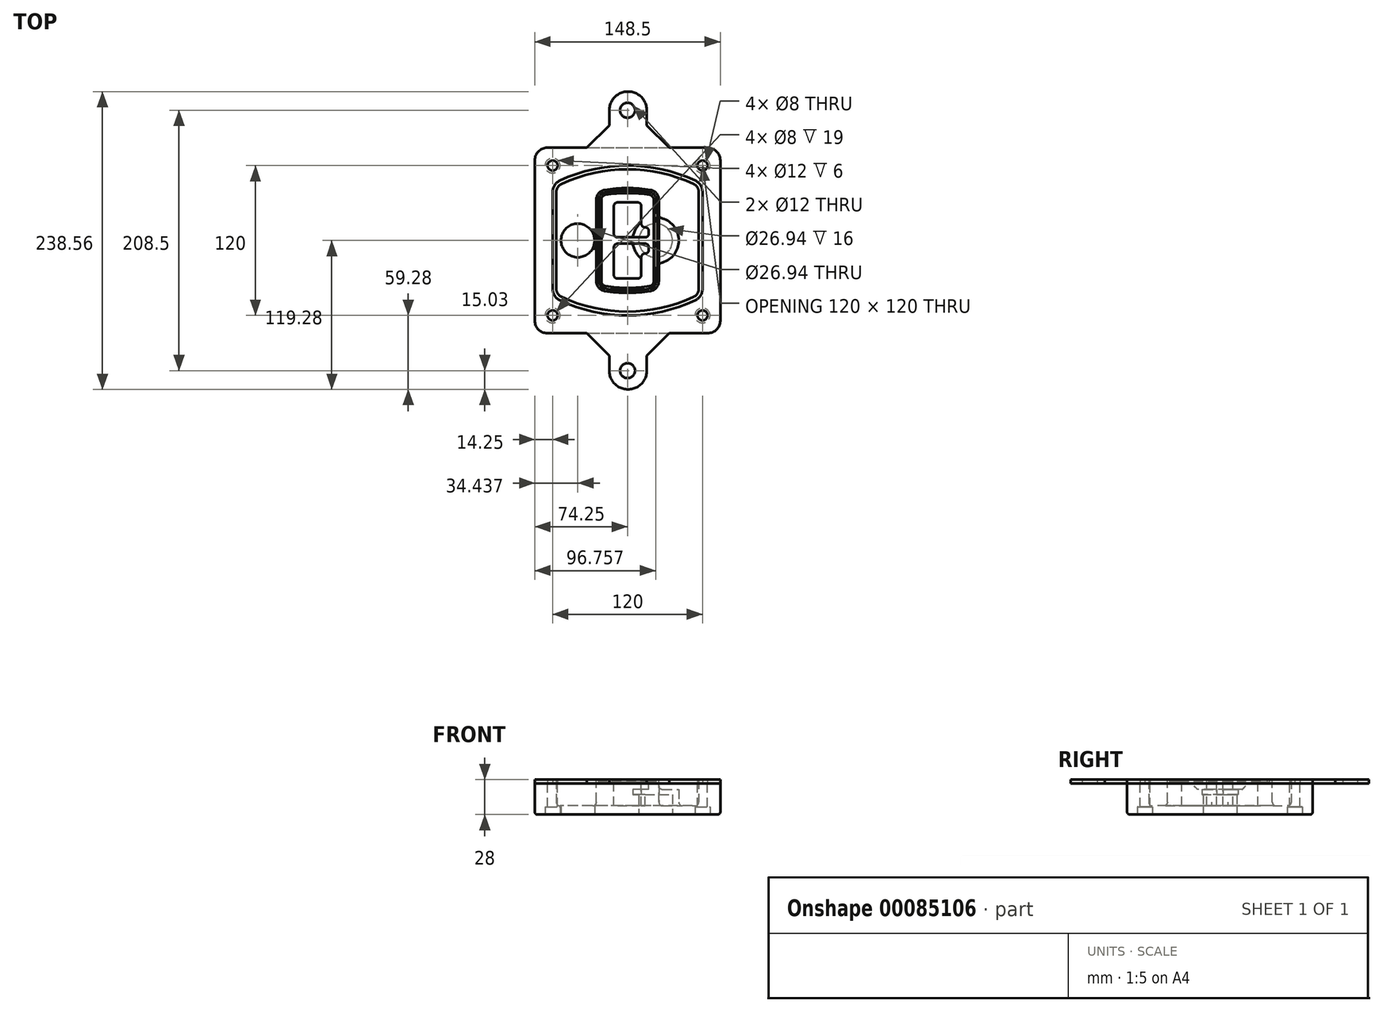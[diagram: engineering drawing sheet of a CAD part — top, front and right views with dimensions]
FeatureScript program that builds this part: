
annotation { "Feature Type Name" : "Feature", "Feature Type Description" : "" }
export const myFeature = defineFeature(function(context is Context, id is Id, definition is map)
    precondition{}
    {
        {
            var Q0;
            Q0=qCreatedBy(makeId("Top.planeOp"),FACE);
            var sketch = newSketch(context, id + "F0", { "sketchPlane" : qUnion([Q0])});
            skPoint(sketch, "E0.rect.middle", {"position": v(0, 0) * mm});
            skLineSegment(sketch, "E1.bottom", {"start": v(-64.25, -74.25) * mm, "end": v(64.25, -74.25) * mm});
            skLineSegment(sketch, "E1.top", {"start": v(-64.25, 74.25) * mm, "end": v(64.25, 74.25) * mm});
            skLineSegment(sketch, "E1.left", {"start": v(-74.25, -64.25) * mm, "end": v(-74.25, 64.25) * mm});
            skLineSegment(sketch, "E1.right", {"start": v(74.25, -64.25) * mm, "end": v(74.25, 64.25) * mm});
            skLineSegment(sketch, "E2", {"start": v(-74.25, 74.25) * mm, "end": v(74.25, -74.25) * mm, "construction": true});
            skLineSegment(sketch, "E3", {"start": v(74.25, 74.25) * mm, "end": v(-74.25, -74.25) * mm, "construction": true});
            skCircle(sketch, "E4", {"center": v(-60, 60) * mm, "radius": 4 * mm});
            skCircle(sketch, "E5", {"center": v(60, 60) * mm, "radius": 4 * mm});
            skCircle(sketch, "E6", {"center": v(60, -60) * mm, "radius": 4 * mm});
            skCircle(sketch, "E7", {"center": v(-60, -60) * mm, "radius": 4 * mm});
            skLineSegment(sketch, "E8", {"start": v(-60, 60) * mm, "end": v(60, 60) * mm, "construction": true});
            skLineSegment(sketch, "E9", {"start": v(60, 60) * mm, "end": v(60, -60) * mm, "construction": true});
            skLineSegment(sketch, "E10", {"start": v(60, -60) * mm, "end": v(-60, -60) * mm, "construction": true});
            skLineSegment(sketch, "E11", {"start": v(-60, -60) * mm, "end": v(-60, 60) * mm, "construction": true});
            skLineSegment(sketch, "E12", {"start": v(-60, 38.83) * mm, "end": v(-60, -38.83) * mm});
            skLineSegment(sketch, "E13", {"start": v(60, 38.83) * mm, "end": v(60, -38.83) * mm});
            skArc(sketch, "E14", {"start": v(54.26, 47.88) * mm, "mid": v(0, 60) * mm, "end": v(-54.26, 47.88) * mm});
            skArc(sketch, "E15", {"start": v(-54.26, -47.88) * mm, "mid": v(0, -60) * mm, "end": v(54.26, -47.88) * mm});
            skLineSegment(sketch, "E16", {"start": v(-60, 0) * mm, "end": v(60, 0) * mm, "construction": true});
            skPoint(sketch, "E17.visualSharp", {"position": v(-60, -45) * mm});
            skArc(sketch, "E17.filletArc", {"start": v(-60, -38.83) * mm, "mid": v(-58.44, -44.2) * mm, "end": v(-54.26, -47.88) * mm});
            skPoint(sketch, "E18.visualSharp", {"position": v(-60, 45) * mm});
            skArc(sketch, "E18.filletArc", {"start": v(-54.26, 47.88) * mm, "mid": v(-58.44, 44.2) * mm, "end": v(-60, 38.83) * mm});
            skPoint(sketch, "E19.visualSharp", {"position": v(60, 45) * mm});
            skArc(sketch, "E19.filletArc", {"start": v(60, 38.83) * mm, "mid": v(58.44, 44.2) * mm, "end": v(54.26, 47.88) * mm});
            skPoint(sketch, "E20.visualSharp", {"position": v(60, -45) * mm});
            skArc(sketch, "E20.filletArc", {"start": v(54.26, -47.88) * mm, "mid": v(58.44, -44.2) * mm, "end": v(60, -38.83) * mm});
            skPoint(sketch, "E21.visualSharp", {"position": v(-74.25, 74.25) * mm});
            skArc(sketch, "E21.filletArc", {"start": v(-64.25, 74.25) * mm, "mid": v(-71.32, 71.32) * mm, "end": v(-74.25, 64.25) * mm});
            skPoint(sketch, "E22.visualSharp", {"position": v(74.25, 74.25) * mm});
            skArc(sketch, "E22.filletArc", {"start": v(74.25, 64.25) * mm, "mid": v(71.32, 71.32) * mm, "end": v(64.25, 74.25) * mm});
            skPoint(sketch, "E23.visualSharp", {"position": v(74.25, -74.25) * mm});
            skArc(sketch, "E23.filletArc", {"start": v(64.25, -74.25) * mm, "mid": v(71.32, -71.32) * mm, "end": v(74.25, -64.25) * mm});
            skPoint(sketch, "E24.visualSharp", {"position": v(-74.25, -74.25) * mm});
            skArc(sketch, "E24.filletArc", {"start": v(-74.25, -64.25) * mm, "mid": v(-71.32, -71.32) * mm, "end": v(-64.25, -74.25) * mm});
            skArc(sketch, "E25.0", {"start": v(57, 38.83) * mm, "mid": v(55.9, 42.58) * mm, "end": v(52.98, 45.17) * mm});
            skLineSegment(sketch, "E25.1", {"start": v(57, 38.83) * mm, "end": v(57, -38.83) * mm});
            skArc(sketch, "E25.2", {"start": v(52.98, -45.17) * mm, "mid": v(55.9, -42.58) * mm, "end": v(57, -38.83) * mm});
            skArc(sketch, "E25.3", {"start": v(-52.98, -45.17) * mm, "mid": v(0, -57) * mm, "end": v(52.98, -45.17) * mm});
            skArc(sketch, "E25.4", {"start": v(-57, -38.83) * mm, "mid": v(-55.9, -42.58) * mm, "end": v(-52.98, -45.17) * mm});
            skArc(sketch, "E25.5", {"start": v(52.98, 45.17) * mm, "mid": v(0, 57) * mm, "end": v(-52.98, 45.17) * mm});
            skLineSegment(sketch, "E25.6", {"start": v(-57, 38.83) * mm, "end": v(-57, -38.83) * mm});
            skArc(sketch, "E25.7", {"start": v(-52.98, 45.17) * mm, "mid": v(-55.9, 42.58) * mm, "end": v(-57, 38.83) * mm});
            skArc(sketch, "E26.0", {"start": v(-55.96, 51.5) * mm, "mid": v(-61.82, 46.33) * mm, "end": v(-64, 38.83) * mm});
            skArc(sketch, "E26.1", {"start": v(55.96, 51.5) * mm, "mid": v(0, 64) * mm, "end": v(-55.96, 51.5) * mm});
            skArc(sketch, "E26.2", {"start": v(64, 38.83) * mm, "mid": v(61.82, 46.33) * mm, "end": v(55.96, 51.5) * mm});
            skLineSegment(sketch, "E26.3", {"start": v(64, 38.83) * mm, "end": v(64, -38.83) * mm});
            skArc(sketch, "E26.4", {"start": v(55.96, -51.5) * mm, "mid": v(61.82, -46.33) * mm, "end": v(64, -38.83) * mm});
            skLineSegment(sketch, "E26.5", {"start": v(-64, 38.83) * mm, "end": v(-64, -38.83) * mm});
            skArc(sketch, "E26.6", {"start": v(-55.96, -51.5) * mm, "mid": v(0, -64) * mm, "end": v(55.96, -51.5) * mm});
            skArc(sketch, "E26.7", {"start": v(-64, -38.83) * mm, "mid": v(-61.82, -46.33) * mm, "end": v(-55.96, -51.5) * mm});
            skSolve(sketch);
        }
        {
            var Q0;
            Q0=makeQuery(id+"F0.imprint","IMPRINT",FACE,{"disambiguationData":[TD([[makeQuery(id+"F0.imprint","IMPRINT",EDGE,{"derivedFrom":sQuery(id+"F0.wireOp",EDGE,"E1.bottom")}),1.0]])]});
            var Q1;
            Q1=makeQuery(id+"F0.imprint","IMPRINT",FACE,{"disambiguationData":[TD([[makeQuery(id+"F0.imprint","IMPRINT",EDGE,{"derivedFrom":sQuery(id+"F0.wireOp",EDGE,"E12")}),1.0]])]});
            var Q2;
            Q2=makeQuery(id+"F0.imprint","IMPRINT",FACE,{"disambiguationData":[TD([[makeQuery(id+"F0.imprint","IMPRINT",EDGE,{"derivedFrom":sQuery(id+"F0.wireOp",EDGE,"E25.0")}),1.0]])]});
            var Q3;
            Q3=makeQuery(id+"F0.imprint","IMPRINT",FACE,{"disambiguationData":[TD([[makeQuery(id+"F0.imprint","IMPRINT",EDGE,{"derivedFrom":sQuery(id+"F0.wireOp",EDGE,"E12")}),-1.0]])]});
            extrude(context, id + "F1", {"entities" : qUnion([Q0, Q1, Q2, Q3]), "oppositeDirection" : true, "depth" : 25 * mm});
        }
        {
            var Q0;
            Q0=makeQuery(id+"F0.imprint","IMPRINT",FACE,{"disambiguationData":[TD([[makeQuery(id+"F0.imprint","IMPRINT",EDGE,{"derivedFrom":sQuery(id+"F0.wireOp",EDGE,"E12")}),1.0]])]});
            extrude(context, id + "F2", {"entities" : qUnion([Q0]), "operationType" : NewBodyOperationType.ADD, "depth" : 3 * mm});
        }
        {
            var Q0;
            Q0=makeQuery(id+"F0.imprint","IMPRINT",FACE,{"disambiguationData":[TD([[makeQuery(id+"F0.imprint","IMPRINT",EDGE,{"derivedFrom":sQuery(id+"F0.wireOp",EDGE,"E25.0")}),1.0]])]});
            extrude(context, id + "F3", {"entities" : qUnion([Q0]), "operationType" : NewBodyOperationType.REMOVE, "oppositeDirection" : true, "depth" : 18 * mm});
        }
        {
            var Q0;
            Q0=makeQuery(id+"F2.opExtrude","CAP_FACE",FACE,{"disambiguationData":[OSD([sQuery(id+"F0.wireOp",EDGE,"E12"),sQuery(id+"F0.wireOp",EDGE,"E13"),sQuery(id+"F0.wireOp",EDGE,"E14"),sQuery(id+"F0.wireOp",EDGE,"E15"),sQuery(id+"F0.wireOp",EDGE,"E17.filletArc"),sQuery(id+"F0.wireOp",EDGE,"E18.filletArc"),sQuery(id+"F0.wireOp",EDGE,"E19.filletArc"),sQuery(id+"F0.wireOp",EDGE,"E20.filletArc"),sQuery(id+"F0.wireOp",EDGE,"E25.0"),sQuery(id+"F0.wireOp",EDGE,"E25.1"),sQuery(id+"F0.wireOp",EDGE,"E25.2"),sQuery(id+"F0.wireOp",EDGE,"E25.3"),sQuery(id+"F0.wireOp",EDGE,"E25.4"),sQuery(id+"F0.wireOp",EDGE,"E25.5"),sQuery(id+"F0.wireOp",EDGE,"E25.6"),sQuery(id+"F0.wireOp",EDGE,"E25.7")])],"isStart":false});
            var sketch = newSketch(context, id + "F4", { "sketchPlane" : qUnion([Q0])});
            skArc(sketch, "E27.0", {"start": v(-18.34, -40.45) * mm, "mid": v(0, -42) * mm, "end": v(18.34, -40.45) * mm});
            skArc(sketch, "E28.0", {"start": v(18.34, 40.45) * mm, "mid": v(0, 42) * mm, "end": v(-18.34, 40.45) * mm});
            skLineSegment(sketch, "E29", {"start": v(-25, 32.57) * mm, "end": v(-25, -32.57) * mm});
            skLineSegment(sketch, "E30", {"start": v(25, 32.57) * mm, "end": v(25, -32.57) * mm});
            skLineSegment(sketch, "E31", {"start": v(-25, 39.1) * mm, "end": v(25, 39.1) * mm, "construction": true});
            skLineSegment(sketch, "E32", {"start": v(-25, -39.1) * mm, "end": v(25, -39.1) * mm, "construction": true});
            skPoint(sketch, "E33.visualSharp", {"position": v(-25, 39.1) * mm});
            skArc(sketch, "E33.filletArc", {"start": v(-18.34, 40.45) * mm, "mid": v(-23.11, 37.73) * mm, "end": v(-25, 32.57) * mm});
            skPoint(sketch, "E34.visualSharp", {"position": v(25, 39.1) * mm});
            skArc(sketch, "E34.filletArc", {"start": v(25, 32.57) * mm, "mid": v(23.11, 37.73) * mm, "end": v(18.34, 40.45) * mm});
            skPoint(sketch, "E35.visualSharp", {"position": v(25, -39.1) * mm});
            skArc(sketch, "E35.filletArc", {"start": v(18.34, -40.45) * mm, "mid": v(23.11, -37.73) * mm, "end": v(25, -32.57) * mm});
            skPoint(sketch, "E36.visualSharp", {"position": v(-25, -39.1) * mm});
            skArc(sketch, "E36.filletArc", {"start": v(-25, -32.57) * mm, "mid": v(-23.11, -37.73) * mm, "end": v(-18.34, -40.45) * mm});
            skArc(sketch, "E37.0", {"start": v(52.98, 45.17) * mm, "mid": v(0, 57) * mm, "end": v(-52.98, 45.17) * mm});
            skArc(sketch, "E37.1", {"start": v(-52.98, 45.17) * mm, "mid": v(-55.9, 42.58) * mm, "end": v(-57, 38.83) * mm});
            skLineSegment(sketch, "E37.2", {"start": v(-57, 38.83) * mm, "end": v(-57, -38.83) * mm});
            skArc(sketch, "E37.3", {"start": v(-57, -38.83) * mm, "mid": v(-55.9, -42.58) * mm, "end": v(-52.98, -45.17) * mm});
            skArc(sketch, "E37.4", {"start": v(-52.98, -45.17) * mm, "mid": v(0, -57) * mm, "end": v(52.98, -45.17) * mm});
            skArc(sketch, "E37.5", {"start": v(52.98, -45.17) * mm, "mid": v(55.9, -42.58) * mm, "end": v(57, -38.83) * mm});
            skLineSegment(sketch, "E37.6", {"start": v(57, 38.83) * mm, "end": v(57, -38.83) * mm});
            skArc(sketch, "E37.7", {"start": v(57, 38.83) * mm, "mid": v(55.9, 42.58) * mm, "end": v(52.98, 45.17) * mm});
            skLineSegment(sketch, "E38.0", {"start": v(23, 32.57) * mm, "end": v(23, -32.57) * mm});
            skArc(sketch, "E38.1", {"start": v(18, -38.48) * mm, "mid": v(21.58, -36.44) * mm, "end": v(23, -32.57) * mm});
            skArc(sketch, "E38.2", {"start": v(-18, -38.48) * mm, "mid": v(0, -40) * mm, "end": v(18, -38.48) * mm});
            skArc(sketch, "E38.3", {"start": v(-23, -32.57) * mm, "mid": v(-21.58, -36.44) * mm, "end": v(-18, -38.48) * mm});
            skLineSegment(sketch, "E38.4", {"start": v(-23, 32.57) * mm, "end": v(-23, -32.57) * mm});
            skArc(sketch, "E38.5", {"start": v(23, 32.57) * mm, "mid": v(21.58, 36.44) * mm, "end": v(18, 38.48) * mm});
            skArc(sketch, "E38.6", {"start": v(-18, 38.48) * mm, "mid": v(-21.58, 36.44) * mm, "end": v(-23, 32.57) * mm});
            skArc(sketch, "E38.7", {"start": v(18, 38.48) * mm, "mid": v(0, 40) * mm, "end": v(-18, 38.48) * mm});
            skArc(sketch, "E39.0", {"start": v(21, 32.57) * mm, "mid": v(20.06, 35.15) * mm, "end": v(17.67, 36.5) * mm});
            skLineSegment(sketch, "E39.1", {"start": v(21, 32.57) * mm, "end": v(21, -32.57) * mm});
            skArc(sketch, "E39.2", {"start": v(17.67, -36.5) * mm, "mid": v(20.06, -35.15) * mm, "end": v(21, -32.57) * mm});
            skArc(sketch, "E39.3", {"start": v(-17.67, -36.5) * mm, "mid": v(0, -38) * mm, "end": v(17.67, -36.5) * mm});
            skArc(sketch, "E39.4", {"start": v(-21, -32.57) * mm, "mid": v(-20.06, -35.15) * mm, "end": v(-17.67, -36.5) * mm});
            skArc(sketch, "E39.5", {"start": v(17.67, 36.5) * mm, "mid": v(0, 38) * mm, "end": v(-17.67, 36.5) * mm});
            skLineSegment(sketch, "E39.6", {"start": v(-21, 32.57) * mm, "end": v(-21, -32.57) * mm});
            skArc(sketch, "E39.7", {"start": v(-17.67, 36.5) * mm, "mid": v(-20.06, 35.15) * mm, "end": v(-21, 32.57) * mm});
            skLineSegment(sketch, "E40", {"start": v(-25, 0) * mm, "end": v(25, 0) * mm, "construction": true});
            skLineSegment(sketch, "E41", {"start": v(-11, 5.5) * mm, "end": v(-11, 27.5) * mm});
            skLineSegment(sketch, "E42", {"start": v(-8, 30.5) * mm, "end": v(8, 30.5) * mm});
            skLineSegment(sketch, "E43", {"start": v(11, 27.5) * mm, "end": v(11, 13.5) * mm});
            skLineSegment(sketch, "E44", {"start": v(14, 10.5) * mm, "end": v(14, 10.5) * mm});
            skLineSegment(sketch, "E45", {"start": v(17, 7.5) * mm, "end": v(17, 5.5) * mm});
            skLineSegment(sketch, "E46", {"start": v(14, 2.5) * mm, "end": v(-8, 2.5) * mm});
            skPoint(sketch, "E47.visualSharp", {"position": v(-11, 30.5) * mm});
            skArc(sketch, "E47.filletArc", {"start": v(-8, 30.5) * mm, "mid": v(-10.12, 29.62) * mm, "end": v(-11, 27.5) * mm});
            skPoint(sketch, "E48.visualSharp", {"position": v(11, 30.5) * mm});
            skArc(sketch, "E48.filletArc", {"start": v(11, 27.5) * mm, "mid": v(10.12, 29.62) * mm, "end": v(8, 30.5) * mm});
            skPoint(sketch, "E49.visualSharp", {"position": v(11, 10.5) * mm});
            skArc(sketch, "E49.filletArc", {"start": v(11, 13.5) * mm, "mid": v(11.88, 11.38) * mm, "end": v(14, 10.5) * mm});
            skPoint(sketch, "E50.visualSharp", {"position": v(17, 10.5) * mm});
            skArc(sketch, "E50.filletArc", {"start": v(17, 7.5) * mm, "mid": v(16.12, 9.62) * mm, "end": v(14, 10.5) * mm});
            skPoint(sketch, "E51.visualSharp", {"position": v(17, 2.5) * mm});
            skArc(sketch, "E51.filletArc", {"start": v(14, 2.5) * mm, "mid": v(16.12, 3.38) * mm, "end": v(17, 5.5) * mm});
            skPoint(sketch, "E52.visualSharp", {"position": v(-11, 2.5) * mm});
            skArc(sketch, "E52.filletArc", {"start": v(-11, 5.5) * mm, "mid": v(-10.12, 3.38) * mm, "end": v(-8, 2.5) * mm});
            skLineSegment(sketch, "E53.0.MirrorCS", {"start": v(14, -2.5) * mm, "end": v(-8, -2.5) * mm});
            skArc(sketch, "E54.0.MirrorCS", {"start": v(-11, -5.5) * mm, "mid": v(-10.12, -3.38) * mm, "end": v(-8, -2.5) * mm});
            skLineSegment(sketch, "E55.0.MirrorCS", {"start": v(-11, -5.5) * mm, "end": v(-11, -27.5) * mm});
            skArc(sketch, "E56.0.MirrorCS", {"start": v(-8, -30.5) * mm, "mid": v(-10.12, -29.62) * mm, "end": v(-11, -27.5) * mm});
            skLineSegment(sketch, "E57.0.MirrorCS", {"start": v(-8, -30.5) * mm, "end": v(8, -30.5) * mm});
            skArc(sketch, "E58.0.MirrorCS", {"start": v(11, -27.5) * mm, "mid": v(10.12, -29.62) * mm, "end": v(8, -30.5) * mm});
            skLineSegment(sketch, "E59.0.MirrorCS", {"start": v(11, -27.5) * mm, "end": v(11, -13.5) * mm});
            skArc(sketch, "E60.0.MirrorCS", {"start": v(11, -13.5) * mm, "mid": v(11.88, -11.38) * mm, "end": v(14, -10.5) * mm});
            skArc(sketch, "E61.0.MirrorCS", {"start": v(17, -7.5) * mm, "mid": v(16.12, -9.62) * mm, "end": v(14, -10.5) * mm});
            skLineSegment(sketch, "E62.0.MirrorCS", {"start": v(17, -7.5) * mm, "end": v(17, -5.5) * mm});
            skArc(sketch, "E63.0.MirrorCS", {"start": v(14, -2.5) * mm, "mid": v(16.12, -3.38) * mm, "end": v(17, -5.5) * mm});
            skSolve(sketch);
        }
        {
            var Q0;
            Q0=makeQuery(id+"F4.imprint","IMPRINT",FACE,{"disambiguationData":[TD([[makeQuery(id+"F4.imprint","IMPRINT",EDGE,{"derivedFrom":sQuery(id+"F4.wireOp",EDGE,"E27.0")}),1.0]])]});
            var Q1;
            Q1=makeQuery(id+"F4.imprint","IMPRINT",FACE,{"disambiguationData":[TD([[makeQuery(id+"F4.imprint","IMPRINT",EDGE,{"derivedFrom":sQuery(id+"F4.wireOp",EDGE,"E38.0")}),-1.0]])]});
            var Q2;
            Q2=makeQuery(id+"F4.imprint","IMPRINT",FACE,{"disambiguationData":[TD([[makeQuery(id+"F4.imprint","IMPRINT",EDGE,{"derivedFrom":sQuery(id+"F4.wireOp",EDGE,"E39.0")}),1.0]])]});
            extrude(context, id + "F5", {"entities" : qUnion([Q0, Q1, Q2]), "operationType" : NewBodyOperationType.ADD, "endBound" : BoundingType.UP_TO_NEXT, "oppositeDirection" : true, "depth" : 25 * mm});
        }
        {
            var Q0;
            Q0=makeQuery(id+"F4.imprint","IMPRINT",FACE,{"disambiguationData":[TD([[makeQuery(id+"F4.imprint","IMPRINT",EDGE,{"derivedFrom":sQuery(id+"F4.wireOp",EDGE,"E38.0")}),-1.0]])]});
            extrude(context, id + "F6", {"entities" : qUnion([Q0]), "operationType" : NewBodyOperationType.REMOVE, "oppositeDirection" : true, "depth" : 2 * mm});
        }
        {
            var Q0;
            Q0=makeQuery(id+"F1.opExtrude","CAP_FACE",FACE,{"disambiguationData":[OSD([sQuery(id+"F0.wireOp",EDGE,"E1.bottom"),sQuery(id+"F0.wireOp",EDGE,"E1.top"),sQuery(id+"F0.wireOp",EDGE,"E1.left"),sQuery(id+"F0.wireOp",EDGE,"E1.right"),sQuery(id+"F0.wireOp",EDGE,"E4"),sQuery(id+"F0.wireOp",EDGE,"E5"),sQuery(id+"F0.wireOp",EDGE,"E6"),sQuery(id+"F0.wireOp",EDGE,"E7"),sQuery(id+"F0.wireOp",EDGE,"E21.filletArc"),sQuery(id+"F0.wireOp",EDGE,"E22.filletArc"),sQuery(id+"F0.wireOp",EDGE,"E23.filletArc"),sQuery(id+"F0.wireOp",EDGE,"E24.filletArc")])],"isStart":false});
            var sketch = newSketch(context, id + "F7", { "sketchPlane" : qUnion([Q0])});
            skCircle(sketch, "E64", {"center": v(22.5, 0) * mm, "radius": 13.47 * mm});
            skCircle(sketch, "E65", {"center": v(-39.81, 0) * mm, "radius": 13.47 * mm});
            skLineSegment(sketch, "E66", {"start": v(74.25, 0) * mm, "end": v(-74.25, 0) * mm});
            skCircle(sketch, "E67", {"center": v(22.5, 0) * mm, "radius": 18.47 * mm});
            skCircle(sketch, "E68", {"center": v(60, -60) * mm, "radius": 6 * mm});
            skCircle(sketch, "E69", {"center": v(-60, -60) * mm, "radius": 6 * mm});
            skCircle(sketch, "E70", {"center": v(-60, 60) * mm, "radius": 6 * mm});
            skCircle(sketch, "E71", {"center": v(60, 60) * mm, "radius": 6 * mm});
            skSolve(sketch);
        }
        {
            var Q0;
            {var subQ1=sQuery(id+"F7.wireOp",EDGE,"E66");var subQ4=sQuery(id+"F7.wireOp",EDGE,"E64");var subQ6=makeQuery(id+"F7.imprint","INTERSECT",VERTEX,{"disambiguationData":[OD(0.0)],"derivedFrom":[subQ4,subQ1]});Q0=makeQuery(id+"F7.imprint","IMPRINT",FACE,{"disambiguationData":[TD([[makeQuery(id+"F7.imprint","IMPRINT",EDGE,{"disambiguationData":[TD([[subQ6,-1.0]])],"derivedFrom":subQ4}),-1.0]])]});}
            var Q1;
            {var subQ0=sQuery(id+"F7.wireOp",EDGE,"E66");var subQ1=sQuery(id+"F7.wireOp",EDGE,"E64");var subQ3=makeQuery(id+"F7.imprint","INTERSECT",VERTEX,{"disambiguationData":[OD(0.0)],"derivedFrom":[subQ1,subQ0]});Q1=makeQuery(id+"F7.imprint","IMPRINT",FACE,{"disambiguationData":[TD([[makeQuery(id+"F7.imprint","IMPRINT",EDGE,{"disambiguationData":[TD([[subQ3,-1.0]])],"derivedFrom":subQ1}),1.0]])]});}
            var Q2;
            {var subQ0=sQuery(id+"F7.wireOp",EDGE,"E66");var subQ1=sQuery(id+"F7.wireOp",EDGE,"E64");var subQ3=makeQuery(id+"F7.imprint","INTERSECT",VERTEX,{"disambiguationData":[OD(0.0)],"derivedFrom":[subQ1,subQ0]});Q2=makeQuery(id+"F7.imprint","IMPRINT",FACE,{"disambiguationData":[TD([[makeQuery(id+"F7.imprint","IMPRINT",EDGE,{"disambiguationData":[TD([[subQ3,1.0]])],"derivedFrom":subQ1}),1.0]])]});}
            var Q3;
            {var subQ1=sQuery(id+"F7.wireOp",EDGE,"E66");var subQ4=sQuery(id+"F7.wireOp",EDGE,"E64");var subQ6=makeQuery(id+"F7.imprint","INTERSECT",VERTEX,{"disambiguationData":[OD(0.0)],"derivedFrom":[subQ4,subQ1]});Q3=makeQuery(id+"F7.imprint","IMPRINT",FACE,{"disambiguationData":[TD([[makeQuery(id+"F7.imprint","IMPRINT",EDGE,{"disambiguationData":[TD([[subQ6,1.0]])],"derivedFrom":subQ4}),-1.0]])]});}
            extrude(context, id + "F8", {"entities" : qUnion([Q0, Q1, Q2, Q3]), "operationType" : NewBodyOperationType.ADD, "oppositeDirection" : true, "depth" : 20 * mm});
        }
        {
            var Q0;
            {var subQ0=sQuery(id+"F7.wireOp",EDGE,"E66");var subQ1=sQuery(id+"F7.wireOp",EDGE,"E64");var subQ3=makeQuery(id+"F7.imprint","INTERSECT",VERTEX,{"disambiguationData":[OD(0.0)],"derivedFrom":[subQ1,subQ0]});Q0=makeQuery(id+"F7.imprint","IMPRINT",FACE,{"disambiguationData":[TD([[makeQuery(id+"F7.imprint","IMPRINT",EDGE,{"disambiguationData":[TD([[subQ3,-1.0]])],"derivedFrom":subQ1}),1.0]])]});}
            var Q1;
            {var subQ0=sQuery(id+"F7.wireOp",EDGE,"E66");var subQ1=sQuery(id+"F7.wireOp",EDGE,"E64");var subQ3=makeQuery(id+"F7.imprint","INTERSECT",VERTEX,{"disambiguationData":[OD(0.0)],"derivedFrom":[subQ1,subQ0]});Q1=makeQuery(id+"F7.imprint","IMPRINT",FACE,{"disambiguationData":[TD([[makeQuery(id+"F7.imprint","IMPRINT",EDGE,{"disambiguationData":[TD([[subQ3,1.0]])],"derivedFrom":subQ1}),1.0]])]});}
            extrude(context, id + "F9", {"entities" : qUnion([Q0, Q1]), "operationType" : NewBodyOperationType.REMOVE, "oppositeDirection" : true, "depth" : 16 * mm});
        }
        {
            var Q0;
            {var subQ0=sQuery(id+"F7.wireOp",EDGE,"E66");var subQ1=sQuery(id+"F7.wireOp",EDGE,"E65");var subQ3=makeQuery(id+"F7.imprint","INTERSECT",VERTEX,{"disambiguationData":[OD(0.0)],"derivedFrom":[subQ1,subQ0]});Q0=makeQuery(id+"F7.imprint","IMPRINT",FACE,{"disambiguationData":[TD([[makeQuery(id+"F7.imprint","IMPRINT",EDGE,{"disambiguationData":[TD([[subQ3,-1.0]])],"derivedFrom":subQ1}),1.0]])]});}
            var Q1;
            {var subQ0=sQuery(id+"F7.wireOp",EDGE,"E66");var subQ1=sQuery(id+"F7.wireOp",EDGE,"E65");var subQ3=makeQuery(id+"F7.imprint","INTERSECT",VERTEX,{"disambiguationData":[OD(0.0)],"derivedFrom":[subQ1,subQ0]});Q1=makeQuery(id+"F7.imprint","IMPRINT",FACE,{"disambiguationData":[TD([[makeQuery(id+"F7.imprint","IMPRINT",EDGE,{"disambiguationData":[TD([[subQ3,1.0]])],"derivedFrom":subQ1}),1.0]])]});}
            extrude(context, id + "F10", {"entities" : qUnion([Q0, Q1]), "operationType" : NewBodyOperationType.REMOVE, "oppositeDirection" : true, "depth" : 25 * mm});
        }
        {
            var Q0;
            Q0=makeQuery(id+"F7.imprint","IMPRINT",FACE,{"disambiguationData":[TD([[makeQuery(id+"F7.imprint","IMPRINT",EDGE,{"derivedFrom":sQuery(id+"F7.wireOp",EDGE,"E68")}),1.0]])]});
            var Q1;
            Q1=makeQuery(id+"F7.imprint","IMPRINT",FACE,{"disambiguationData":[TD([[makeQuery(id+"F7.imprint","IMPRINT",EDGE,{"derivedFrom":makeQuery(id+"F1.opExtrude","CAP_EDGE",EDGE,{"disambiguationData":[OSD([sQuery(id+"F0.wireOp",EDGE,"E5")])],"isStart":false})}),-1.0]])]});
            var Q2;
            Q2=makeQuery(id+"F7.imprint","IMPRINT",FACE,{"disambiguationData":[TD([[makeQuery(id+"F7.imprint","IMPRINT",EDGE,{"derivedFrom":sQuery(id+"F7.wireOp",EDGE,"E69")}),1.0]])]});
            var Q3;
            Q3=makeQuery(id+"F7.imprint","IMPRINT",FACE,{"disambiguationData":[TD([[makeQuery(id+"F7.imprint","IMPRINT",EDGE,{"derivedFrom":makeQuery(id+"F1.opExtrude","CAP_EDGE",EDGE,{"disambiguationData":[OSD([sQuery(id+"F0.wireOp",EDGE,"E4")])],"isStart":false})}),-1.0]])]});
            var Q4;
            Q4=makeQuery(id+"F7.imprint","IMPRINT",FACE,{"disambiguationData":[TD([[makeQuery(id+"F7.imprint","IMPRINT",EDGE,{"derivedFrom":sQuery(id+"F7.wireOp",EDGE,"E70")}),1.0]])]});
            var Q5;
            Q5=makeQuery(id+"F7.imprint","IMPRINT",FACE,{"disambiguationData":[TD([[makeQuery(id+"F7.imprint","IMPRINT",EDGE,{"derivedFrom":makeQuery(id+"F1.opExtrude","CAP_EDGE",EDGE,{"disambiguationData":[OSD([sQuery(id+"F0.wireOp",EDGE,"E7")])],"isStart":false})}),-1.0]])]});
            var Q6;
            Q6=makeQuery(id+"F7.imprint","IMPRINT",FACE,{"disambiguationData":[TD([[makeQuery(id+"F7.imprint","IMPRINT",EDGE,{"derivedFrom":sQuery(id+"F7.wireOp",EDGE,"E71")}),1.0]])]});
            var Q7;
            Q7=makeQuery(id+"F7.imprint","IMPRINT",FACE,{"disambiguationData":[TD([[makeQuery(id+"F7.imprint","IMPRINT",EDGE,{"derivedFrom":makeQuery(id+"F1.opExtrude","CAP_EDGE",EDGE,{"disambiguationData":[OSD([sQuery(id+"F0.wireOp",EDGE,"E6")])],"isStart":false})}),-1.0]])]});
            extrude(context, id + "F11", {"entities" : qUnion([Q0, Q1, Q2, Q3, Q4, Q5, Q6, Q7]), "operationType" : NewBodyOperationType.REMOVE, "oppositeDirection" : true, "depth" : 6 * mm});
        }
        {
            var Q0;
            Q0=makeQuery(id+"F9.boolean.opBoolean","COPY",FACE,{"derivedFrom":makeQuery(id+"F9.opExtrude","CAP_FACE",FACE,{"disambiguationData":[OSD([sQuery(id+"F7.wireOp",EDGE,"E64")])],"isStart":false})});
            var sketch = newSketch(context, id + "F12", { "sketchPlane" : qUnion([Q0])});
            skArc(sketch, "E72.0", {"start": v(11, 14.45) * mm, "mid": v(6.45, 9.13) * mm, "end": v(4.2, 2.5) * mm});
            skArc(sketch, "E72.1", {"start": v(4.2, -2.5) * mm, "mid": v(6.45, -9.13) * mm, "end": v(11, -14.45) * mm});
            skLineSegment(sketch, "E73", {"start": v(4.2, -2.5) * mm, "end": v(14, -2.5) * mm});
            skLineSegment(sketch, "E74.0", {"start": v(14, 2.5) * mm, "end": v(4.2, 2.5) * mm});
            skArc(sketch, "E74.1", {"start": v(14, 2.5) * mm, "mid": v(16.12, 3.38) * mm, "end": v(17, 5.5) * mm});
            skLineSegment(sketch, "E74.2", {"start": v(17, 7.5) * mm, "end": v(17, 5.5) * mm});
            skArc(sketch, "E74.3", {"start": v(17, 7.5) * mm, "mid": v(16.12, 9.62) * mm, "end": v(14, 10.5) * mm});
            skArc(sketch, "E74.4", {"start": v(11, 13.5) * mm, "mid": v(11.88, 11.38) * mm, "end": v(14, 10.5) * mm});
            skLineSegment(sketch, "E74.5", {"start": v(11, 14.45) * mm, "end": v(11, 13.5) * mm});
            skLineSegment(sketch, "E74.7", {"start": v(14, -2.5) * mm, "end": v(4.2, -2.5) * mm});
            skArc(sketch, "E74.8", {"start": v(14, -2.5) * mm, "mid": v(16.12, -3.38) * mm, "end": v(17, -5.5) * mm});
            skLineSegment(sketch, "E74.9", {"start": v(17, -7.5) * mm, "end": v(17, -5.5) * mm});
            skArc(sketch, "E74.10", {"start": v(17, -7.5) * mm, "mid": v(16.12, -9.62) * mm, "end": v(14, -10.5) * mm});
            skArc(sketch, "E74.11", {"start": v(11, -13.5) * mm, "mid": v(11.88, -11.38) * mm, "end": v(14, -10.5) * mm});
            skLineSegment(sketch, "E74.12", {"start": v(11, -14.45) * mm, "end": v(11, -13.5) * mm});
            skPoint(sketch, "E75.orphan", {"position": v(11, -27.5) * mm});
            skPoint(sketch, "E76.orphan", {"position": v(-8, -2.5) * mm});
            skPoint(sketch, "E77.orphan", {"position": v(-8, 2.5) * mm});
            skPoint(sketch, "E78.orphan", {"position": v(11, 27.5) * mm});
            skSolve(sketch);
        }
        {
            var Q0;
            {var subQ7=sQuery(id+"F12.wireOp",EDGE,"E72.0");var subQ14=sQuery(id+"F12.wireOp",EDGE,"E72.1");var subQ16=sQuery(id+"F12.wireOp",EDGE,"E74.1");var subQ18=sQuery(id+"F12.wireOp",EDGE,"E74.8");Q0=qUnion([makeQuery(id+"F12.imprint","IMPRINT",FACE,{"disambiguationData":[TD([[makeQuery(id+"F12.imprint","IMPRINT",EDGE,{"derivedFrom":subQ7}),1.0]])]}),makeQuery(id+"F12.imprint","IMPRINT",FACE,{"disambiguationData":[TD([[makeQuery(id+"F12.imprint","IMPRINT",EDGE,{"derivedFrom":subQ14}),1.0]])]}),makeQuery(id+"F12.imprint","IMPRINT",FACE,{"disambiguationData":[TD([[makeQuery(id+"F12.imprint","IMPRINT",EDGE,{"derivedFrom":subQ16}),1.0]])]}),makeQuery(id+"F12.imprint","IMPRINT",FACE,{"disambiguationData":[TD([[makeQuery(id+"F12.imprint","IMPRINT",EDGE,{"derivedFrom":subQ18}),-1.0]])]})]);}
            var Q1;
            Q1=makeQuery(id+"F5.boolean.opBoolean","SPLIT",FACE,{"disambiguationData":[TD([makeQuery(id+"F5.opExtrude","SWEPT_FACE",FACE,{"disambiguationData":[OSD([sQuery(id+"F4.wireOp",EDGE,"E41")])]})])],"derivedFrom":makeQuery(id+"F3.boolean.opBoolean","COPY",FACE,{"derivedFrom":makeQuery(id+"F3.opExtrude","CAP_FACE",FACE,{"disambiguationData":[OSD([sQuery(id+"F0.wireOp",EDGE,"E25.0"),sQuery(id+"F0.wireOp",EDGE,"E25.1"),sQuery(id+"F0.wireOp",EDGE,"E25.2"),sQuery(id+"F0.wireOp",EDGE,"E25.3"),sQuery(id+"F0.wireOp",EDGE,"E25.4"),sQuery(id+"F0.wireOp",EDGE,"E25.5"),sQuery(id+"F0.wireOp",EDGE,"E25.6"),sQuery(id+"F0.wireOp",EDGE,"E25.7")])],"isStart":false})})});
            extrude(context, id + "F13", {"entities" : qUnion([Q0]), "operationType" : NewBodyOperationType.REMOVE, "endBound" : BoundingType.UP_TO_SURFACE, "endBoundEntityFace" : qUnion([Q1]), "depth" : 25 * mm});
        }
        {
            var Q0;
            Q0=makeQuery(id+"F3.boolean.opBoolean","COPY",EDGE,{"derivedFrom":makeQuery(id+"F3.opExtrude","CAP_EDGE",EDGE,{"disambiguationData":[OSD([sQuery(id+"F0.wireOp",EDGE,"E25.6")])],"isStart":false})});
            var Q1;
            Q1=makeQuery(id+"F8.boolean.opBoolean","INTERSECT",EDGE,{"derivedFrom":[makeQuery(id+"F5.opExtrude","SWEPT_FACE",FACE,{"disambiguationData":[OSD([sQuery(id+"F4.wireOp",EDGE,"E30")])]}),makeQuery(id+"F8.opExtrude","CAP_FACE",FACE,{"disambiguationData":[OSD([sQuery(id+"F7.wireOp",EDGE,"E67")])],"isStart":false})]});
            var Q2;
            Q2=makeQuery(id+"F8.boolean.opBoolean","INTERSECT",EDGE,{"disambiguationData":[OD(1.0)],"derivedFrom":[makeQuery(id+"F5.opExtrude","SWEPT_FACE",FACE,{"disambiguationData":[OSD([sQuery(id+"F4.wireOp",EDGE,"E30")])]}),makeQuery(id+"F8.opExtrude","SWEPT_FACE",FACE,{"disambiguationData":[OSD([sQuery(id+"F7.wireOp",EDGE,"E67")])]})]});
            var Q3;
            {var subQ0=sQuery(id+"F4.wireOp",EDGE,"E30");Q3=makeQuery(id+"F8.boolean.opBoolean","SPLIT",EDGE,{"disambiguationData":[TD([makeQuery(id+"F5.opExtrude","SWEPT_FACE",FACE,{"disambiguationData":[OSD([sQuery(id+"F4.wireOp",EDGE,"E35.filletArc")])]})])],"derivedFrom":makeQuery(id+"F5.opExtrude","CAP_EDGE",EDGE,{"disambiguationData":[OSD([subQ0])],"isStart":false})});}
            var Q4;
            {var subQ0=sQuery(id+"F0.wireOp",EDGE,"E25.7");var subQ1=sQuery(id+"F0.wireOp",EDGE,"E25.1");var subQ2=sQuery(id+"F0.wireOp",EDGE,"E25.6");var subQ3=sQuery(id+"F0.wireOp",EDGE,"E25.5");var subQ4=sQuery(id+"F0.wireOp",EDGE,"E25.4");var subQ5=sQuery(id+"F0.wireOp",EDGE,"E25.0");var subQ6=sQuery(id+"F0.wireOp",EDGE,"E25.2");var subQ7=sQuery(id+"F0.wireOp",EDGE,"E25.3");Q4=makeQuery(id+"F8.boolean.opBoolean","INTERSECT",EDGE,{"derivedFrom":[makeQuery(id+"F5.boolean.opBoolean","SPLIT",FACE,{"disambiguationData":[TD([makeQuery(id+"F2.opExtrude","SWEPT_FACE",FACE,{"disambiguationData":[OSD([subQ5])]})])],"derivedFrom":makeQuery(id+"F3.boolean.opBoolean","COPY",FACE,{"derivedFrom":makeQuery(id+"F3.opExtrude","CAP_FACE",FACE,{"disambiguationData":[OSD([subQ5,subQ1,subQ6,subQ7,subQ4,subQ3,subQ2,subQ0])],"isStart":false})})}),makeQuery(id+"F8.opExtrude","SWEPT_FACE",FACE,{"disambiguationData":[OSD([sQuery(id+"F7.wireOp",EDGE,"E67")])]})]});}
            var Q5;
            Q5=makeQuery(id+"F8.boolean.opBoolean","INTERSECT",EDGE,{"disambiguationData":[OD(0.0)],"derivedFrom":[makeQuery(id+"F5.opExtrude","SWEPT_FACE",FACE,{"disambiguationData":[OSD([sQuery(id+"F4.wireOp",EDGE,"E30")])]}),makeQuery(id+"F8.opExtrude","SWEPT_FACE",FACE,{"disambiguationData":[OSD([sQuery(id+"F7.wireOp",EDGE,"E67")])]})]});
            fillet(context, id + "F14", {"entities" : qUnion([Q0, Q1, Q2, Q3, Q4, Q5]), "radius" : 3 * mm, "tangentPropagation" : true, "allowEdgeOverflow" : false});
        }
        {
            var Q0;
            Q0=makeQuery(id+"F1.opExtrude","CAP_EDGE",EDGE,{"disambiguationData":[OSD([sQuery(id+"F0.wireOp",EDGE,"E1.bottom")])],"isStart":false});
            fillet(context, id + "F15", {"entities" : qUnion([Q0]), "radius" : 2 * mm, "tangentPropagation" : true, "allowEdgeOverflow" : false});
        }
        {
            var Q0;
            {var subQ0=sQuery(id+"F0.wireOp",EDGE,"E22.filletArc");var subQ1=sQuery(id+"F0.wireOp",EDGE,"E7");var subQ2=sQuery(id+"F0.wireOp",EDGE,"E6");var subQ3=sQuery(id+"F0.wireOp",EDGE,"E5");var subQ4=sQuery(id+"F0.wireOp",EDGE,"E4");var subQ5=sQuery(id+"F0.wireOp",EDGE,"E1.bottom");var subQ6=sQuery(id+"F0.wireOp",EDGE,"E21.filletArc");var subQ7=sQuery(id+"F0.wireOp",EDGE,"E1.top");var subQ8=sQuery(id+"F0.wireOp",EDGE,"E1.left");var subQ9=sQuery(id+"F0.wireOp",EDGE,"E1.right");var subQ10=sQuery(id+"F0.wireOp",EDGE,"E23.filletArc");var subQ11=sQuery(id+"F0.wireOp",EDGE,"E24.filletArc");Q0=makeQuery(id+"F2.boolean.opBoolean","SPLIT",FACE,{"disambiguationData":[TD([makeQuery(id+"F1.opExtrude","SWEPT_FACE",FACE,{"disambiguationData":[OSD([subQ5])]})])],"derivedFrom":makeQuery(id+"F1.opExtrude","CAP_FACE",FACE,{"disambiguationData":[OSD([subQ5,subQ7,subQ8,subQ9,subQ4,subQ3,subQ2,subQ1,subQ6,subQ0,subQ10,subQ11])],"isStart":true})});}
            var sketch = newSketch(context, id + "F16", { "sketchPlane" : qUnion([Q0])});
            skLineSegment(sketch, "E79.0", {"start": v(-64.25, 74.25) * mm, "end": v(64.25, 74.25) * mm});
            skArc(sketch, "E79.1", {"start": v(-64.25, 74.25) * mm, "mid": v(-71.32, 71.32) * mm, "end": v(-74.25, 64.25) * mm});
            skLineSegment(sketch, "E79.2", {"start": v(-74.25, -64.25) * mm, "end": v(-74.25, 64.25) * mm});
            skArc(sketch, "E79.3", {"start": v(-74.25, -64.25) * mm, "mid": v(-71.32, -71.32) * mm, "end": v(-64.25, -74.25) * mm});
            skLineSegment(sketch, "E79.4", {"start": v(-64.25, -74.25) * mm, "end": v(64.25, -74.25) * mm});
            skArc(sketch, "E79.5", {"start": v(64.25, -74.25) * mm, "mid": v(71.32, -71.32) * mm, "end": v(74.25, -64.25) * mm});
            skLineSegment(sketch, "E79.6", {"start": v(74.25, -64.25) * mm, "end": v(74.25, 64.25) * mm});
            skArc(sketch, "E79.7", {"start": v(74.25, 64.25) * mm, "mid": v(71.32, 71.32) * mm, "end": v(64.25, 74.25) * mm});
            skCircle(sketch, "E79.8", {"center": v(60, 60) * mm, "radius": 4 * mm});
            skArc(sketch, "E79.9", {"start": v(54.26, 47.88) * mm, "mid": v(0, 60) * mm, "end": v(-54.26, 47.88) * mm});
            skArc(sketch, "E79.10", {"start": v(60, 38.83) * mm, "mid": v(58.44, 44.2) * mm, "end": v(54.26, 47.88) * mm});
            skLineSegment(sketch, "E79.11", {"start": v(60, 38.83) * mm, "end": v(60, -38.83) * mm});
            skArc(sketch, "E79.12", {"start": v(54.26, -47.88) * mm, "mid": v(58.44, -44.2) * mm, "end": v(60, -38.83) * mm});
            skArc(sketch, "E79.13", {"start": v(-54.26, -47.88) * mm, "mid": v(0, -60) * mm, "end": v(54.26, -47.88) * mm});
            skArc(sketch, "E79.14", {"start": v(-60, -38.83) * mm, "mid": v(-58.44, -44.2) * mm, "end": v(-54.26, -47.88) * mm});
            skLineSegment(sketch, "E79.15", {"start": v(-60, 38.83) * mm, "end": v(-60, -38.83) * mm});
            skArc(sketch, "E79.16", {"start": v(-54.26, 47.88) * mm, "mid": v(-58.44, 44.2) * mm, "end": v(-60, 38.83) * mm});
            skCircle(sketch, "E79.17", {"center": v(-60, 60) * mm, "radius": 4 * mm});
            skCircle(sketch, "E79.18", {"center": v(-60, -60) * mm, "radius": 4 * mm});
            skCircle(sketch, "E79.19", {"center": v(60, -60) * mm, "radius": 4 * mm});
            skCircle(sketch, "E80", {"center": v(0, 104.25) * mm, "radius": 6 * mm});
            skLineSegment(sketch, "E81", {"start": v(0, 74.25) * mm, "end": v(0, 104.25) * mm, "construction": true});
            skArc(sketch, "E82", {"start": v(15.4, 104.25) * mm, "mid": v(0.4, 119.28) * mm, "end": v(-14.6, 104.25) * mm});
            skLineSegment(sketch, "E83", {"start": v(15.4, 104.25) * mm, "end": v(15.4, 92.25) * mm});
            skLineSegment(sketch, "E84", {"start": v(15.4, 92.25) * mm, "end": v(33.4, 74.25) * mm});
            skLineSegment(sketch, "E85", {"start": v(-14.6, 104.25) * mm, "end": v(-14.58, 92.25) * mm});
            skLineSegment(sketch, "E86", {"start": v(-14.58, 92.25) * mm, "end": v(-32.58, 74.25) * mm});
            skLineSegment(sketch, "E87", {"start": v(-74.25, 0) * mm, "end": v(74.25, 0) * mm, "construction": true});
            skLineSegment(sketch, "E88.MirrorCS", {"start": v(15.4, -92.25) * mm, "end": v(33.4, -74.25) * mm});
            skLineSegment(sketch, "E89.MirrorCS", {"start": v(15.4, -104.25) * mm, "end": v(15.4, -92.25) * mm});
            skArc(sketch, "E90.MirrorCS", {"start": v(15.4, -104.25) * mm, "mid": v(0.4, -119.28) * mm, "end": v(-14.6, -104.25) * mm});
            skLineSegment(sketch, "E91.MirrorCS", {"start": v(-14.6, -104.25) * mm, "end": v(-14.58, -92.25) * mm});
            skLineSegment(sketch, "E92.MirrorCS", {"start": v(-14.58, -92.25) * mm, "end": v(-32.58, -74.25) * mm});
            skLineSegment(sketch, "E93.MirrorCS", {"start": v(0, -74.25) * mm, "end": v(0, -104.25) * mm, "construction": true});
            skCircle(sketch, "E94.MirrorC", {"center": v(0, -104.25) * mm, "radius": 6 * mm});
            skLineSegment(sketch, "E95", {"start": v(-32.58, 74.25) * mm, "end": v(33.4, 74.25) * mm});
            skLineSegment(sketch, "E96", {"start": v(33.4, -74.25) * mm, "end": v(-32.58, -74.25) * mm});
            skSolve(sketch);
        }
        {
            var Q0;
            Q0=makeQuery(id+"F16.imprint","IMPRINT",FACE,{"disambiguationData":[TD([[makeQuery(id+"F16.imprint","IMPRINT",EDGE,{"derivedFrom":sQuery(id+"F16.wireOp",EDGE,"E80")}),-1.0]])]});
            var Q1;
            Q1=makeQuery(id+"F16.imprint","IMPRINT",FACE,{"disambiguationData":[TD([[makeQuery(id+"F16.imprint","IMPRINT",EDGE,{"derivedFrom":sQuery(id+"F16.wireOp",EDGE,"E88.MirrorCS")}),1.0]])]});
            var Q2;
            {var subQ0=sQuery(id+"F16.wireOp",EDGE,"E79.1");Q2=makeQuery(id+"F16.imprint","IMPRINT",FACE,{"disambiguationData":[TD([[makeQuery(id+"F16.imprint","IMPRINT",EDGE,{"derivedFrom":subQ0}),1.0]])]});}
            var Q3;
            {var subQ0=sQuery(id+"F4.wireOp",EDGE,"E63.0.MirrorCS");var subQ1=sQuery(id+"F4.wireOp",EDGE,"E62.0.MirrorCS");var subQ2=sQuery(id+"F4.wireOp",EDGE,"E61.0.MirrorCS");var subQ3=sQuery(id+"F4.wireOp",EDGE,"E60.0.MirrorCS");var subQ4=sQuery(id+"F4.wireOp",EDGE,"E59.0.MirrorCS");var subQ5=sQuery(id+"F4.wireOp",EDGE,"E58.0.MirrorCS");var subQ6=sQuery(id+"F4.wireOp",EDGE,"E57.0.MirrorCS");var subQ7=sQuery(id+"F4.wireOp",EDGE,"E56.0.MirrorCS");var subQ8=sQuery(id+"F4.wireOp",EDGE,"E55.0.MirrorCS");var subQ9=sQuery(id+"F4.wireOp",EDGE,"E54.0.MirrorCS");var subQ10=sQuery(id+"F4.wireOp",EDGE,"E53.0.MirrorCS");var subQ11=sQuery(id+"F4.wireOp",EDGE,"E52.filletArc");var subQ12=sQuery(id+"F4.wireOp",EDGE,"E45");var subQ13=sQuery(id+"F4.wireOp",EDGE,"E43");var subQ14=sQuery(id+"F4.wireOp",EDGE,"E42");var subQ15=sQuery(id+"F4.wireOp",EDGE,"E41");var subQ16=sQuery(id+"F4.wireOp",EDGE,"E46");var subQ17=sQuery(id+"F4.wireOp",EDGE,"E47.filletArc");var subQ18=sQuery(id+"F4.wireOp",EDGE,"E48.filletArc");var subQ19=sQuery(id+"F4.wireOp",EDGE,"E49.filletArc");var subQ20=sQuery(id+"F4.wireOp",EDGE,"E50.filletArc");var subQ21=sQuery(id+"F4.wireOp",EDGE,"E51.filletArc");Q3=makeQuery(id+"F6.boolean.opBoolean","SPLIT",FACE,{"disambiguationData":[TD([makeQuery(id+"F5.opExtrude","SWEPT_FACE",FACE,{"disambiguationData":[OSD([subQ15])]})])],"derivedFrom":makeQuery(id+"F5.opExtrude","CAP_FACE",FACE,{"disambiguationData":[OSD([sQuery(id+"F4.wireOp",EDGE,"E27.0"),sQuery(id+"F4.wireOp",EDGE,"E28.0"),sQuery(id+"F4.wireOp",EDGE,"E29"),sQuery(id+"F4.wireOp",EDGE,"E30"),sQuery(id+"F4.wireOp",EDGE,"E33.filletArc"),sQuery(id+"F4.wireOp",EDGE,"E34.filletArc"),sQuery(id+"F4.wireOp",EDGE,"E35.filletArc"),sQuery(id+"F4.wireOp",EDGE,"E36.filletArc"),subQ15,subQ14,subQ13,subQ12,subQ16,subQ17,subQ18,subQ19,subQ20,subQ21,subQ11,subQ10,subQ9,subQ8,subQ7,subQ6,subQ5,subQ4,subQ3,subQ2,subQ1,subQ0])],"isStart":true})});}
            extrude(context, id + "F17", {"entities" : qUnion([Q0, Q1, Q2]), "endBound" : BoundingType.UP_TO_SURFACE, "endBoundEntityFace" : qUnion([Q3]), "depth" : 25 * mm});
        }
    });
